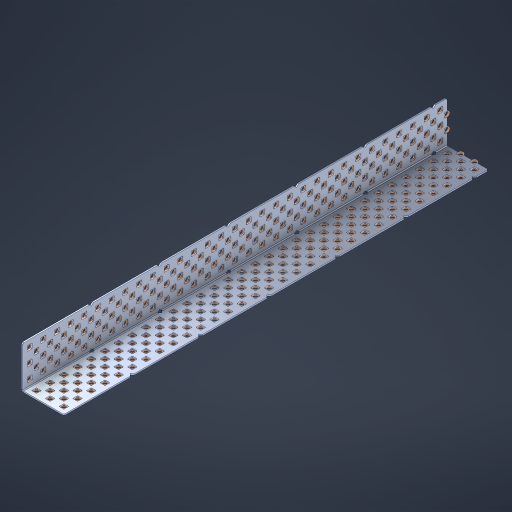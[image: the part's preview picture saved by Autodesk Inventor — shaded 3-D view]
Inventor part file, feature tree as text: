
AUTODESK INVENTOR PART (.ipt)
format: ipt  version: 2023 (Build 270158000, 158)  size: 3,101,696 bytes
history: native  units: in
note: dims shown in document units (in); Inventor stores cm internally (conversion verified against a paired STEP export)
features: other x316, extrude x308, sheet_metal_op x8, sketch x7, pattern_linear x3, mirror x1, chamfer x1
ambient origin geometry x8: Origin, YZ Plane, XZ Plane, XY Plane, X Axis, Y Axis, Z Axis, Center Point
bodies: Solid1 (feature_tree), Body (feature_tree)
feature tree (644):
  sheet_metal_op  "Flanges"
  sheet_metal_op  "Body Pattern"
  pattern_linear  "Center Double"  Spacing1=1.5in  [1 undecoded]
  pattern_linear  "Center Pattern"  Spacing1=0.1875in  [1 undecoded]
  other  "Arc Length"
  pattern_linear  "Notch Pattern"  Spacing1=0.0469in  [1 undecoded]
  other  "Diagonal Plane"
  mirror  "Everything Mirrored"
  chamfer  "End Chamfer"
  sketch  "Sketch1"  dims[d0=1.5in]
  other  "Plate1"
  sketch  "Sketch2"  dims[d1=15.5in]
  other  "Plate2"
  sheet_metal_op  "Bend1"
  sheet_metal_op  "Corner1"
  sketch  "Sketch8"  dims[d2=0.0469in]
  sketch  "Sketch9"  dims[d3=0.0469in]
  other  "Srf91"
  sheet_metal_op  "Body Pattern Sketch"
  other  "Srf92"
  sketch  "Sketch13"  dims[d4=0.0234in]
  sketch  "Sketch15"  dims[d5=0.0938in]
  sketch  "Sketch16"  dims[d6=0.0469in d7=1.5in d8=90.0deg d9=0.0312in d10=0.1875in d11=0.0469in d12=0.0469in d49=0.182in d50=0.02in d52=0.25in d53=0.0469in d54=0.0in d55=0.172in d56=1.0in d57=0.0in d85=0.1473in d86=0.1659in d89=0.0469in d90=0.0in d91=0.04in d92=0.0491in d95=2.5in d96=0.04in d97=0.25in d98=45.0deg d106=0.182in d107=0.02in d110=0.0469in d111=0.0in d112=0.172in d113=0.5in d114=0.0in d117=0.5in d126=0.0491in d127=0.1227in d128=0.08in d129=0.04in d130=2.5in d131=0.25in d132=12.2047in d134=0.5in d135=1.1811in d137=0.5in d140=0.5in d141=1.0in d142=0.3937in d144=0.5in d145=0.071in d146=0.7874in d148=0.5in]
  other  "Srf786"
  other  "Srf856"
  other  "Srf889"
  other  "Srf890"
  other  "Srf891"
  other  "Srf1275"
  other  "Srf1276"
  other  "Srf1278"
  other  "Srf1277"
  other  "Srf1285"
  other  "Srf1286"
  other  "Srf1287"
  other  "Srf1445"
  other  "Srf1446"
  other  "Srf1447"
  other  "Srf1448"
  other  "Srf1449"
  other  "Srf1537"
  other  "Srf1538"
  other  "Srf1539"
  other  "Srf1540"
  other  "Srf1541"
  other  "Srf1807"
  other  "Srf1808"
  other  "Srf1809"
  other  "Srf1810"
  other  "Srf1811"
  other  "Srf1812"
  other  "Srf1813"
  other  "Srf1814"
  other  "Srf1815"
  other  "Srf1816"
  other  "Srf1817"
  other  "Srf1818"
  other  "Srf1819"
  other  "Srf1820"
  other  "Srf1821"
  other  "Srf1822"
  other  "Srf1823"
  other  "Srf1824"
  other  "Srf1825"
  other  "Srf1826"
  other  "Srf1827"
  other  "Srf1828"
  other  "Srf1959"
  other  "Srf1960"
  other  "Srf1961"
  other  "Srf1962"
  other  "Srf1963"
  other  "Srf1964"
  other  "Srf1965"
  other  "Srf1966"
  other  "Srf1967"
  other  "Srf1968"
  other  "Srf1969"
  other  "Srf1970"
  other  "Srf1971"
  other  "Srf1972"
  other  "Srf1973"
  other  "Srf1974"
  other  "Srf1975"
  other  "Srf1976"
  other  "Srf1977"
  other  "Srf1978"
  other  "Srf1979"
  other  "Srf1980"
  other  "Srf2009"
  other  "Srf2010"
  other  "Srf2011"
  other  "Srf2012"
  other  "Srf2013"
  other  "Srf2014"
  other  "Srf2015"
  other  "Srf2016"
  other  "Srf2017"
  other  "Srf2018"
  other  "Srf2019"
  other  "Srf2020"
  other  "Srf2021"
  other  "Srf2022"
  other  "Srf2023"
  other  "Srf2024"
  other  "Srf2025"
  other  "Srf2026"
  other  "Srf2027"
  other  "Srf2028"
  other  "Srf2029"
  other  "Srf2030"
  other  "Srf2031"
  other  "Srf2032"
  other  "Srf2033"
  other  "Srf2034"
  other  "Srf2035"
  other  "Srf2036"
  other  "Srf2037"
  other  "Srf2038"
  other  "Srf2039"
  other  "Srf2043"
  other  "Srf2044"
  other  "Srf2045"
  other  "Srf2046"
  other  "Srf2047"
  other  "Srf2048"
  other  "Srf2049"
  other  "Srf2050"
  other  "Srf2051"
  other  "Srf2052"
  other  "Srf2053"
  other  "Srf2054"
  other  "Srf2055"
  other  "Srf2056"
  other  "Srf2057"
  other  "Srf2058"
  other  "Srf2059"
  other  "Srf2060"
  other  "Srf2061"
  other  "Srf2062"
  other  "Srf2063"
  other  "Srf2064"
  other  "Srf2065"
  other  "Srf2066"
  other  "Srf2067"
  other  "Srf2068"
  other  "Srf2069"
  other  "Srf2070"
  other  "Srf2071"
  other  "Srf2072"
  other  "Srf2076"
  other  "Srf2077"
  other  "Srf2078"
  other  "Srf2079"
  other  "Srf2080"
  other  "Srf2081"
  other  "Srf2082"
  other  "Srf2083"
  other  "Srf2084"
  other  "Srf2085"
  other  "Srf2086"
  other  "Srf2087"
  other  "Srf2088"
  other  "Srf2089"
  other  "Srf2090"
  other  "Srf2091"
  other  "Srf2092"
  other  "Srf2093"
  other  "Srf2094"
  other  "Srf2095"
  other  "Srf2096"
  other  "Srf2097"
  other  "Srf2098"
  other  "Srf2099"
  other  "Srf2100"
  other  "Srf2101"
  other  "Srf2102"
  other  "Srf2103"
  other  "Srf2104"
  other  "Srf2105"
  other  "Srf2106"
  other  "Srf2107"
  other  "Srf2108"
  other  "Srf2109"
  other  "Srf2110"
  other  "Srf2111"
  other  "Srf2112"
  other  "Srf2113"
  other  "Srf2114"
  other  "Srf2115"
  other  "Srf2116"
  other  "Srf2117"
  other  "Srf2118"
  other  "Srf2119"
  other  "Srf2120"
  other  "Srf2121"
  other  "Srf2122"
  other  "Srf2123"
  other  "Srf2124"
  other  "Srf2125"
  other  "Srf2126"
  other  "Srf2127"
  other  "Srf2128"
  other  "Srf2129"
  other  "Srf2130"
  other  "Srf2131"
  other  "Srf2132"
  other  "Srf2133"
  other  "Srf2134"
  other  "Srf2135"
  other  "Srf2136"
  other  "Srf2137"
  other  "Srf2138"
  other  "Srf2139"
  other  "Srf2140"
  other  "Srf2141"
  other  "Srf2142"
  other  "Srf2143"
  other  "Srf2144"
  other  "Srf2145"
  other  "Srf2146"
  other  "Srf2147"
  other  "Srf2148"
  other  "Srf2149"
  other  "Srf2150"
  other  "Srf2151"
  other  "Srf2152"
  other  "Srf2153"
  other  "Srf2154"
  other  "Srf2155"
  other  "Srf2156"
  other  "Srf2157"
  other  "Srf2158"
  other  "Srf2159"
  other  "Srf2160"
  other  "Srf2161"
  other  "Srf2162"
  other  "Srf2163"
  other  "Srf2164"
  other  "Srf2165"
  other  "Srf2166"
  other  "Srf2179"
  other  "Srf2180"
  other  "Srf2181"
  other  "Srf2182"
  other  "Srf2183"
  other  "Srf2184"
  other  "Srf2185"
  other  "Srf2186"
  other  "Srf2187"
  other  "Srf2188"
  other  "Srf2189"
  other  "Srf2190"
  other  "Srf2191"
  other  "Srf2192"
  other  "Srf2193"
  other  "Srf2194"
  other  "Srf2195"
  other  "Srf2196"
  other  "Srf2197"
  other  "Srf2198"
  other  "Srf2199"
  other  "Srf2200"
  other  "Srf2201"
  other  "Srf2202"
  other  "Srf2203"
  other  "Srf2204"
  other  "Srf2205"
  other  "Srf2206"
  other  "Srf2207"
  other  "Srf2208"
  other  "Srf2209"
  other  "Srf2210"
  other  "Srf2211"
  other  "Srf2212"
  other  "Srf2213"
  other  "Srf2214"
  other  "Srf2215"
  other  "Srf2216"
  other  "Srf2217"
  other  "Srf2218"
  other  "Srf2219"
  other  "Srf2220"
  other  "Srf2221"
  other  "Srf2222"
  other  "Srf2223"
  other  "Srf2224"
  other  "Srf2225"
  other  "Srf2226"
  other  "Srf2227"
  other  "Srf2228"
  other  "Srf2229"
  other  "Srf2230"
  other  "Srf2231"
  other  "Srf2232"
  other  "Srf2233"
  other  "Srf2234"
  other  "Srf2235"
  other  "Srf2236"
  other  "Srf2237"
  other  "Srf2238"
  other  "Srf2239"
  other  "Srf2240"
  other  "Srf2241"
  other  "Srf2242"
  other  "Srf2243"
  other  "Srf2244"
  other  "Srf2245"
  other  "Srf2246"
  other  "Srf2247"
  other  "Srf2248"
  other  "Srf2249"
  other  "Srf2250"
  other  "Srf2251"
  other  "Srf2252"
  other  "Srf2253"
  other  "Srf2254"
  other  "Srf2255"
  other  "Srf2256"
  other  "Srf2257"
  other  "Srf2258"
  other  "Srf2259"
  other  "Srf2260"
  other  "Srf2261"
  other  "Srf2262"
  other  "Srf2263"
  other  "Srf2264"
  other  "Srf2265"
  other  "Srf2266"
  other  "Srf2267"
  other  "Srf2268"
  sheet_metal_op  "Body Stamp"
  sheet_metal_op  "Body Circle"
  other  "Center Stamp"
  other  "Center Circle"
  sheet_metal_op  "Notch"
  extrude  "ExtrusionSrf92"  Depth=0.0469in
  extrude  "ExtrusionSrf856"  Depth=0.182in
  extrude  "ExtrusionSrf889"  Depth=0.02in
  extrude  "ExtrusionSrf890"  Depth=0.25in
  extrude  "ExtrusionSrf891"  Depth=0.0469in
  extrude  "ExtrusionSrf1275"  TaperAngle=0.0deg  [1 undecoded]
  extrude  "ExtrusionSrf1276"  Depth=0.5in
  extrude  "ExtrusionSrf1277"  Depth=1.0in TaperAngle=0.0deg
  extrude  "ExtrusionSrf1345"  Depth=0.5in
  extrude  "ExtrusionSrf1346"  Depth=0.5in
  extrude  "ExtrusionSrf1347"  Depth=0.0469in
  extrude  "ExtrusionSrf1348"  Depth=0.5in TaperAngle=0.0deg
  extrude  "ExtrusionSrf1445"  Depth=0.5in
  extrude  "ExtrusionSrf1446"  Depth=0.25in TaperAngle=45.0deg
  extrude  "ExtrusionSrf1447"  Depth=0.182in
  extrude  "ExtrusionSrf1448"  Depth=0.02in
  extrude  "ExtrusionSrf1449"  Depth=0.0469in
  extrude  "ExtrusionSrf1537"  TaperAngle=0.0deg  [1 undecoded]
  extrude  "ExtrusionSrf1538"  Depth=0.5in
  extrude  "ExtrusionSrf1539"  Depth=0.5in TaperAngle=0.0deg
  extrude  "ExtrusionSrf1540"  Depth=0.5in
  extrude  "ExtrusionSrf1541"  Depth=0.5in
  extrude  "ExtrusionSrf1807"  Depth=0.5in
  extrude  "ExtrusionSrf1808"  Depth=0.5in
  extrude  "ExtrusionSrf1809"  Depth=0.5in
  extrude  "ExtrusionSrf1810"  Depth=0.5in
  extrude  "ExtrusionSrf1811"  Depth=0.25in
  extrude  "ExtrusionSrf1812"  Depth=0.5in
  extrude  "ExtrusionSrf1813"  Depth=0.5in
  extrude  "ExtrusionSrf1814"  Depth=0.5in
  extrude  "ExtrusionSrf1815"  Depth=1.0in
  extrude  "ExtrusionSrf1816"  Depth=0.3937in
  extrude  "ExtrusionSrf1817"  Depth=0.5in
  extrude  "ExtrusionSrf1818"  Depth=0.5in
  extrude  "ExtrusionSrf1819"  [1 undecoded]
  extrude  "ExtrusionSrf1820"  [1 undecoded]
  extrude  "ExtrusionSrf1821"  [1 undecoded]
  extrude  "ExtrusionSrf1822"  [1 undecoded]
  extrude  "ExtrusionSrf1823"  [1 undecoded]
  extrude  "ExtrusionSrf1824"  [1 undecoded]
  extrude  "ExtrusionSrf1825"  [1 undecoded]
  extrude  "ExtrusionSrf1826"  [1 undecoded]
  extrude  "ExtrusionSrf1827"  [1 undecoded]
  extrude  "ExtrusionSrf1828"  [1 undecoded]
  extrude  "ExtrusionSrf1959"  [1 undecoded]
  extrude  "ExtrusionSrf1960"  [1 undecoded]
  extrude  "ExtrusionSrf1961"  [1 undecoded]
  extrude  "ExtrusionSrf1962"  [1 undecoded]
  extrude  "ExtrusionSrf1963"  [1 undecoded]
  extrude  "ExtrusionSrf1964"  [1 undecoded]
  extrude  "ExtrusionSrf1965"  [1 undecoded]
  extrude  "ExtrusionSrf1966"  [1 undecoded]
  extrude  "ExtrusionSrf1967"  [1 undecoded]
  extrude  "ExtrusionSrf1968"  [1 undecoded]
  extrude  "ExtrusionSrf1969"  [1 undecoded]
  extrude  "ExtrusionSrf1970"  [1 undecoded]
  extrude  "ExtrusionSrf1971"  [1 undecoded]
  extrude  "ExtrusionSrf1972"  [1 undecoded]
  extrude  "ExtrusionSrf1973"  [1 undecoded]
  extrude  "ExtrusionSrf1974"  [1 undecoded]
  extrude  "ExtrusionSrf1975"  [1 undecoded]
  extrude  "ExtrusionSrf1976"  [1 undecoded]
  extrude  "ExtrusionSrf1977"  [1 undecoded]
  extrude  "ExtrusionSrf1978"  [1 undecoded]
  extrude  "ExtrusionSrf1979"  [1 undecoded]
  extrude  "ExtrusionSrf1980"  [1 undecoded]
  extrude  "ExtrusionSrf2009"  [1 undecoded]
  extrude  "ExtrusionSrf2010"  [1 undecoded]
  extrude  "ExtrusionSrf2011"  [1 undecoded]
  extrude  "ExtrusionSrf2012"  [1 undecoded]
  extrude  "ExtrusionSrf2013"  [1 undecoded]
  extrude  "ExtrusionSrf2014"  [1 undecoded]
  extrude  "ExtrusionSrf2015"  [1 undecoded]
  extrude  "ExtrusionSrf2016"  [1 undecoded]
  extrude  "ExtrusionSrf2017"  [1 undecoded]
  extrude  "ExtrusionSrf2018"  [1 undecoded]
  extrude  "ExtrusionSrf2019"  [1 undecoded]
  extrude  "ExtrusionSrf2020"  [1 undecoded]
  extrude  "ExtrusionSrf2021"  [1 undecoded]
  extrude  "ExtrusionSrf2022"  [1 undecoded]
  extrude  "ExtrusionSrf2023"  [1 undecoded]
  extrude  "ExtrusionSrf2024"  [1 undecoded]
  extrude  "ExtrusionSrf2025"  [1 undecoded]
  extrude  "ExtrusionSrf2026"  [1 undecoded]
  extrude  "ExtrusionSrf2027"  [1 undecoded]
  extrude  "ExtrusionSrf2028"  [1 undecoded]
  extrude  "ExtrusionSrf2029"  [1 undecoded]
  extrude  "ExtrusionSrf2030"  [1 undecoded]
  extrude  "ExtrusionSrf2031"  [1 undecoded]
  extrude  "ExtrusionSrf2032"  [1 undecoded]
  extrude  "ExtrusionSrf2033"  [1 undecoded]
  extrude  "ExtrusionSrf2034"  [1 undecoded]
  extrude  "ExtrusionSrf2035"  [1 undecoded]
  extrude  "ExtrusionSrf2036"  [1 undecoded]
  extrude  "ExtrusionSrf2037"  [1 undecoded]
  extrude  "ExtrusionSrf2038"  [1 undecoded]
  extrude  "ExtrusionSrf2039"  [1 undecoded]
  extrude  "ExtrusionSrf2043"  [1 undecoded]
  extrude  "ExtrusionSrf2044"  [1 undecoded]
  extrude  "ExtrusionSrf2045"  [1 undecoded]
  extrude  "ExtrusionSrf2046"  [1 undecoded]
  extrude  "ExtrusionSrf2047"  [1 undecoded]
  extrude  "ExtrusionSrf2048"  [1 undecoded]
  extrude  "ExtrusionSrf2049"  [1 undecoded]
  extrude  "ExtrusionSrf2050"  [1 undecoded]
  extrude  "ExtrusionSrf2051"  [1 undecoded]
  extrude  "ExtrusionSrf2052"  [1 undecoded]
  extrude  "ExtrusionSrf2053"  [1 undecoded]
  extrude  "ExtrusionSrf2054"  [1 undecoded]
  extrude  "ExtrusionSrf2055"  [1 undecoded]
  extrude  "ExtrusionSrf2056"  [1 undecoded]
  extrude  "ExtrusionSrf2057"  [1 undecoded]
  extrude  "ExtrusionSrf2058"  [1 undecoded]
  extrude  "ExtrusionSrf2059"  [1 undecoded]
  extrude  "ExtrusionSrf2060"  [1 undecoded]
  extrude  "ExtrusionSrf2061"  [1 undecoded]
  extrude  "ExtrusionSrf2062"  [1 undecoded]
  extrude  "ExtrusionSrf2063"  [1 undecoded]
  extrude  "ExtrusionSrf2064"  [1 undecoded]
  extrude  "ExtrusionSrf2065"  [1 undecoded]
  extrude  "ExtrusionSrf2066"  [1 undecoded]
  extrude  "ExtrusionSrf2067"  [1 undecoded]
  extrude  "ExtrusionSrf2068"  [1 undecoded]
  extrude  "ExtrusionSrf2069"  [1 undecoded]
  extrude  "ExtrusionSrf2070"  [1 undecoded]
  extrude  "ExtrusionSrf2071"  [1 undecoded]
  extrude  "ExtrusionSrf2072"  [1 undecoded]
  extrude  "ExtrusionSrf2076"  [1 undecoded]
  extrude  "ExtrusionSrf2077"  [1 undecoded]
  extrude  "ExtrusionSrf2078"  [1 undecoded]
  extrude  "ExtrusionSrf2079"  [1 undecoded]
  extrude  "ExtrusionSrf2080"  [1 undecoded]
  extrude  "ExtrusionSrf2081"  [1 undecoded]
  extrude  "ExtrusionSrf2082"  [1 undecoded]
  extrude  "ExtrusionSrf2083"  [1 undecoded]
  extrude  "ExtrusionSrf2084"  [1 undecoded]
  extrude  "ExtrusionSrf2085"  [1 undecoded]
  extrude  "ExtrusionSrf2086"  [1 undecoded]
  extrude  "ExtrusionSrf2087"  [1 undecoded]
  extrude  "ExtrusionSrf2088"  [1 undecoded]
  extrude  "ExtrusionSrf2089"  [1 undecoded]
  extrude  "ExtrusionSrf2090"  [1 undecoded]
  extrude  "ExtrusionSrf2091"  [1 undecoded]
  extrude  "ExtrusionSrf2092"  [1 undecoded]
  extrude  "ExtrusionSrf2093"  [1 undecoded]
  extrude  "ExtrusionSrf2094"  [1 undecoded]
  extrude  "ExtrusionSrf2095"  [1 undecoded]
  extrude  "ExtrusionSrf2096"  [1 undecoded]
  extrude  "ExtrusionSrf2097"  [1 undecoded]
  extrude  "ExtrusionSrf2098"  [1 undecoded]
  extrude  "ExtrusionSrf2099"  [1 undecoded]
  extrude  "ExtrusionSrf2100"  [1 undecoded]
  extrude  "ExtrusionSrf2101"  [1 undecoded]
  extrude  "ExtrusionSrf2102"  [1 undecoded]
  extrude  "ExtrusionSrf2103"  [1 undecoded]
  extrude  "ExtrusionSrf2104"  [1 undecoded]
  extrude  "ExtrusionSrf2105"  [1 undecoded]
  extrude  "ExtrusionSrf2106"  [1 undecoded]
  extrude  "ExtrusionSrf2107"  [1 undecoded]
  extrude  "ExtrusionSrf2108"  [1 undecoded]
  extrude  "ExtrusionSrf2109"  [1 undecoded]
  extrude  "ExtrusionSrf2110"  [1 undecoded]
  extrude  "ExtrusionSrf2111"  [1 undecoded]
  extrude  "ExtrusionSrf2112"  [1 undecoded]
  extrude  "ExtrusionSrf2113"  [1 undecoded]
  extrude  "ExtrusionSrf2114"  [1 undecoded]
  extrude  "ExtrusionSrf2115"  [1 undecoded]
  extrude  "ExtrusionSrf2116"  [1 undecoded]
  extrude  "ExtrusionSrf2117"  [1 undecoded]
  extrude  "ExtrusionSrf2118"  [1 undecoded]
  extrude  "ExtrusionSrf2119"  [1 undecoded]
  extrude  "ExtrusionSrf2120"  [1 undecoded]
  extrude  "ExtrusionSrf2121"  [1 undecoded]
  extrude  "ExtrusionSrf2122"  [1 undecoded]
  extrude  "ExtrusionSrf2123"  [1 undecoded]
  extrude  "ExtrusionSrf2124"  [1 undecoded]
  extrude  "ExtrusionSrf2125"  [1 undecoded]
  extrude  "ExtrusionSrf2126"  [1 undecoded]
  extrude  "ExtrusionSrf2127"  [1 undecoded]
  extrude  "ExtrusionSrf2128"  [1 undecoded]
  extrude  "ExtrusionSrf2129"  [1 undecoded]
  extrude  "ExtrusionSrf2130"  [1 undecoded]
  extrude  "ExtrusionSrf2131"  [1 undecoded]
  extrude  "ExtrusionSrf2132"  [1 undecoded]
  extrude  "ExtrusionSrf2133"  [1 undecoded]
  extrude  "ExtrusionSrf2134"  [1 undecoded]
  extrude  "ExtrusionSrf2135"  [1 undecoded]
  extrude  "ExtrusionSrf2136"  [1 undecoded]
  extrude  "ExtrusionSrf2137"  [1 undecoded]
  extrude  "ExtrusionSrf2138"  [1 undecoded]
  extrude  "ExtrusionSrf2139"  [1 undecoded]
  extrude  "ExtrusionSrf2140"  [1 undecoded]
  extrude  "ExtrusionSrf2141"  [1 undecoded]
  extrude  "ExtrusionSrf2142"  [1 undecoded]
  extrude  "ExtrusionSrf2143"  [1 undecoded]
  extrude  "ExtrusionSrf2144"  [1 undecoded]
  extrude  "ExtrusionSrf2145"  [1 undecoded]
  extrude  "ExtrusionSrf2146"  [1 undecoded]
  extrude  "ExtrusionSrf2147"  [1 undecoded]
  extrude  "ExtrusionSrf2148"  [1 undecoded]
  extrude  "ExtrusionSrf2149"  [1 undecoded]
  extrude  "ExtrusionSrf2150"  [1 undecoded]
  extrude  "ExtrusionSrf2151"  [1 undecoded]
  extrude  "ExtrusionSrf2152"  [1 undecoded]
  extrude  "ExtrusionSrf2153"  [1 undecoded]
  extrude  "ExtrusionSrf2154"  [1 undecoded]
  extrude  "ExtrusionSrf2155"  [1 undecoded]
  extrude  "ExtrusionSrf2156"  [1 undecoded]
  extrude  "ExtrusionSrf2157"  [1 undecoded]
  extrude  "ExtrusionSrf2158"  [1 undecoded]
  extrude  "ExtrusionSrf2159"  [1 undecoded]
  extrude  "ExtrusionSrf2160"  [1 undecoded]
  extrude  "ExtrusionSrf2161"  [1 undecoded]
  extrude  "ExtrusionSrf2162"  [1 undecoded]
  extrude  "ExtrusionSrf2163"  [1 undecoded]
  extrude  "ExtrusionSrf2164"  [1 undecoded]
  extrude  "ExtrusionSrf2165"  [1 undecoded]
  extrude  "ExtrusionSrf2166"  [1 undecoded]
  extrude  "ExtrusionSrf2179"  [1 undecoded]
  extrude  "ExtrusionSrf2180"  [1 undecoded]
  extrude  "ExtrusionSrf2181"  [1 undecoded]
  extrude  "ExtrusionSrf2182"  [1 undecoded]
  extrude  "ExtrusionSrf2183"  [1 undecoded]
  extrude  "ExtrusionSrf2184"  [1 undecoded]
  extrude  "ExtrusionSrf2185"  [1 undecoded]
  extrude  "ExtrusionSrf2186"  [1 undecoded]
  extrude  "ExtrusionSrf2187"  [1 undecoded]
  extrude  "ExtrusionSrf2188"  [1 undecoded]
  extrude  "ExtrusionSrf2189"  [1 undecoded]
  extrude  "ExtrusionSrf2190"  [1 undecoded]
  extrude  "ExtrusionSrf2191"  [1 undecoded]
  extrude  "ExtrusionSrf2192"  [1 undecoded]
  extrude  "ExtrusionSrf2193"  [1 undecoded]
  extrude  "ExtrusionSrf2194"  [1 undecoded]
  extrude  "ExtrusionSrf2195"  [1 undecoded]
  extrude  "ExtrusionSrf2196"  [1 undecoded]
  extrude  "ExtrusionSrf2197"  [1 undecoded]
  extrude  "ExtrusionSrf2198"  [1 undecoded]
  extrude  "ExtrusionSrf2199"  [1 undecoded]
  extrude  "ExtrusionSrf2200"  [1 undecoded]
  extrude  "ExtrusionSrf2201"  [1 undecoded]
  extrude  "ExtrusionSrf2202"  [1 undecoded]
  extrude  "ExtrusionSrf2203"  [1 undecoded]
  extrude  "ExtrusionSrf2204"  [1 undecoded]
  extrude  "ExtrusionSrf2205"  [1 undecoded]
  extrude  "ExtrusionSrf2206"  [1 undecoded]
  extrude  "ExtrusionSrf2207"  [1 undecoded]
  extrude  "ExtrusionSrf2208"  [1 undecoded]
  extrude  "ExtrusionSrf2209"  [1 undecoded]
  extrude  "ExtrusionSrf2210"  [1 undecoded]
  extrude  "ExtrusionSrf2211"  [1 undecoded]
  extrude  "ExtrusionSrf2212"  [1 undecoded]
  extrude  "ExtrusionSrf2213"  [1 undecoded]
  extrude  "ExtrusionSrf2214"  [1 undecoded]
  extrude  "ExtrusionSrf2215"  [1 undecoded]
  extrude  "ExtrusionSrf2216"  [1 undecoded]
  extrude  "ExtrusionSrf2217"  [1 undecoded]
  extrude  "ExtrusionSrf2218"  [1 undecoded]
  extrude  "ExtrusionSrf2219"  [1 undecoded]
  extrude  "ExtrusionSrf2220"  [1 undecoded]
  extrude  "ExtrusionSrf2221"  [1 undecoded]
  extrude  "ExtrusionSrf2222"  [1 undecoded]
  extrude  "ExtrusionSrf2223"  [1 undecoded]
  extrude  "ExtrusionSrf2224"  [1 undecoded]
  extrude  "ExtrusionSrf2225"  [1 undecoded]
  extrude  "ExtrusionSrf2226"  [1 undecoded]
  extrude  "ExtrusionSrf2227"  [1 undecoded]
  extrude  "ExtrusionSrf2228"  [1 undecoded]
  extrude  "ExtrusionSrf2229"  [1 undecoded]
  extrude  "ExtrusionSrf2230"  [1 undecoded]
  extrude  "ExtrusionSrf2231"  [1 undecoded]
  extrude  "ExtrusionSrf2232"  [1 undecoded]
  extrude  "ExtrusionSrf2233"  [1 undecoded]
  extrude  "ExtrusionSrf2234"  [1 undecoded]
  extrude  "ExtrusionSrf2235"  [1 undecoded]
  extrude  "ExtrusionSrf2236"  [1 undecoded]
  extrude  "ExtrusionSrf2237"  [1 undecoded]
  extrude  "ExtrusionSrf2238"  [1 undecoded]
  extrude  "ExtrusionSrf2239"  [1 undecoded]
  extrude  "ExtrusionSrf2240"  [1 undecoded]
  extrude  "ExtrusionSrf2241"  [1 undecoded]
  extrude  "ExtrusionSrf2242"  [1 undecoded]
  extrude  "ExtrusionSrf2243"  [1 undecoded]
  extrude  "ExtrusionSrf2244"  [1 undecoded]
  extrude  "ExtrusionSrf2245"  [1 undecoded]
  extrude  "ExtrusionSrf2246"  [1 undecoded]
  extrude  "ExtrusionSrf2247"  [1 undecoded]
  extrude  "ExtrusionSrf2248"  [1 undecoded]
  extrude  "ExtrusionSrf2249"  [1 undecoded]
  extrude  "ExtrusionSrf2250"  [1 undecoded]
  extrude  "ExtrusionSrf2251"  [1 undecoded]
  extrude  "ExtrusionSrf2252"  [1 undecoded]
  extrude  "ExtrusionSrf2253"  [1 undecoded]
  extrude  "ExtrusionSrf2254"  [1 undecoded]
  extrude  "ExtrusionSrf2255"  [1 undecoded]
  extrude  "ExtrusionSrf2256"  [1 undecoded]
  extrude  "ExtrusionSrf2257"  [1 undecoded]
  extrude  "ExtrusionSrf2258"  [1 undecoded]
  extrude  "ExtrusionSrf2259"  [1 undecoded]
  extrude  "ExtrusionSrf2260"  [1 undecoded]
  extrude  "ExtrusionSrf2261"  [1 undecoded]
  extrude  "ExtrusionSrf2262"  [1 undecoded]
  extrude  "ExtrusionSrf2263"  [1 undecoded]
  extrude  "ExtrusionSrf2264"  [1 undecoded]
  extrude  "ExtrusionSrf2265"  [1 undecoded]
  extrude  "ExtrusionSrf2266"  [1 undecoded]
  extrude  "ExtrusionSrf2267"  [1 undecoded]
  extrude  "ExtrusionSrf2268"  [1 undecoded]
note: 279 required parameter values undecoded (feature->parameter linkage not recoverable at this tier; creation-order binding heuristic only, values carry confidence <= 0.55)
